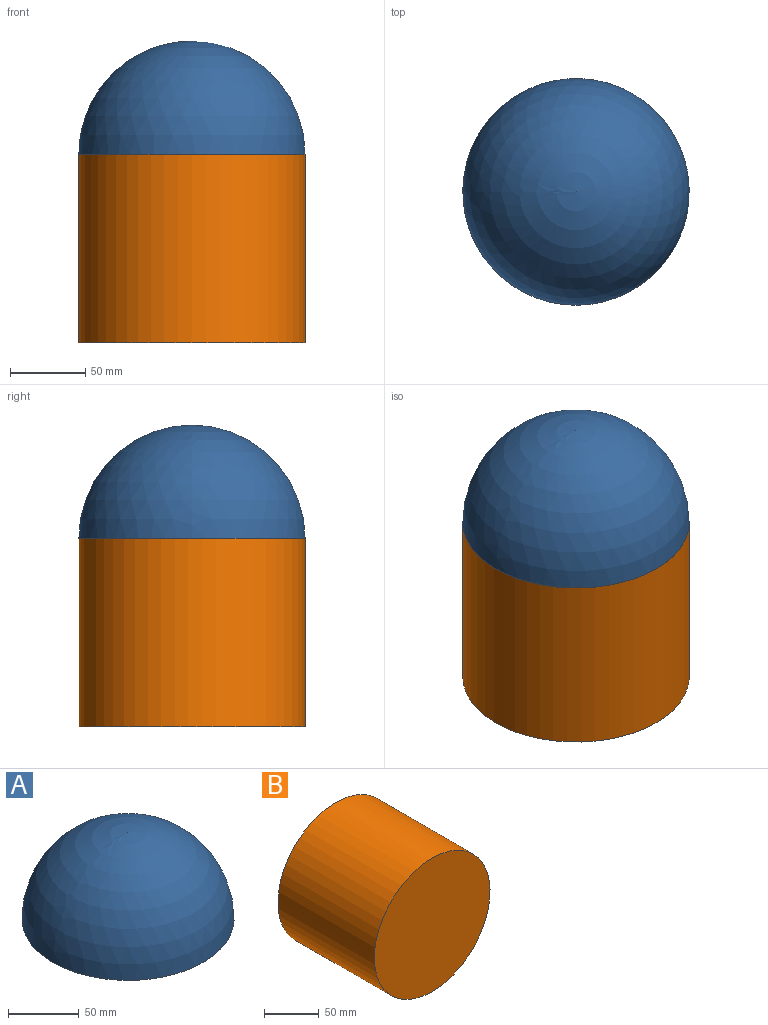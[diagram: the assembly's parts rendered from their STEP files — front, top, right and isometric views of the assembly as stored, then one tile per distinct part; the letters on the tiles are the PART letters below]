
ASSEMBLY  parts=2 mates=1
PART A: 2 faces, bbox 150x150x75 mm
  f0: plane 150x150mm, normal (0,0,-1), area 17671.5mm2, adj f1
  f1: sphere r=75mm, area 35342.9mm2, adj f0
PART B: 3 faces, bbox 150x125x150 mm
  f0: cylinder r=75mm len=150mm, axis (0,1,0), area 58904.9mm2, adj f1,f2
  f1: plane 150x150mm, normal (0,-1,0), area 17671.5mm2, adj f0
  f2: plane 150x150mm, normal (0,1,0), area 17671.5mm2, adj f0
PLACE A t=(-92.06,-3.86,-38.57)mm
PLACE B rot(axis=(-1,0,0),90deg) t=(-92.06,-3.86,-163.57)mm
MATE fastened B.f0 <-> A.f0  axis (0,0,1) through (-92.06,-3.86,-38.57)mm
